# Revit family: P1E_2963-2962-2606_OS275
name_source: partatom
category: Porte
units: mm (PartAtom-declared; Revit-internal decimal feet)

## family parameters
Condiviso = No
Host = Muro
Numero OmniClass = 23.30.10.00
Punto di calcolo locali = No
Sempre verticale = Sì
Taglio con vuoti quando caricato = No
Titolo OmniClass = Doors

## types (4) — shared parameters
Altezza = 2500 mm  [stored 8.2021 ft]
Chiusura muro = Per host
Costruzione analitica = <Nessuno>
Descrizione = Porta ad un'anta, apertura esterna
Funzione = Interno
H = 2500 mm  [stored 8.2021 ft]
H1 = 2500 mm  [stored 8.2021 ft]
H_Max = 2900 mm
H_Min = 1600 mm
H_maniglia = 1000 mm  [stored 3.28084 ft]
H_vetro = 2424 mm  [stored 7.95276 ft]
L_Max = 1000 mm  [stored 3.28084 ft]
L_Min = 400 mm  [stored 1.31234 ft]
Larghezza telaio = 75 mm
Modello = OS2 75
Produttore = Secco Sistemi Spa
Proiezione telaio est. = 25 mm  [stored 0.082021 ft]
Proiezione telaio int. = 25 mm  [stored 0.082021 ft]
URL = https://www.seccosistemi.com
n2_cerniere = 2
n3_cerniere = 3
n4_cerniere = 4
numero_cerniere = 3

## per-type parameters (varying)
| type | L | L1 | L_vetro | Larghezza | MATERIALE | WARNING |
| Acciaio zincato | 1000 mm  [stored 3.28084 ft] | 1000 mm  [stored 3.28084 ft] | 924 mm  [stored 3.0315 ft] | 1100 mm | Acciaio | Sì |
| Acciaio inox | 1000 mm  [stored 3.28084 ft] | 1000 mm  [stored 3.28084 ft] | 924 mm  [stored 3.0315 ft] | 1100 mm | Acciaio inox, spazzolato | Sì |
| Acciaio Corten | 900 mm  [stored 2.95276 ft] | 900 mm  [stored 2.95276 ft] | 824 mm  [stored 2.70341 ft] | 900 mm  [stored 2.95276 ft] | Acciaio corten | No |
| Ottone | 1000 mm  [stored 3.28084 ft] | 1000 mm  [stored 3.28084 ft] | 924 mm  [stored 3.0315 ft] | 1100 mm | Ottone | Sì |

note: [stored X ft] marks values corroborated as IEEE doubles in the binary element streams (Revit-internal decimal feet)
